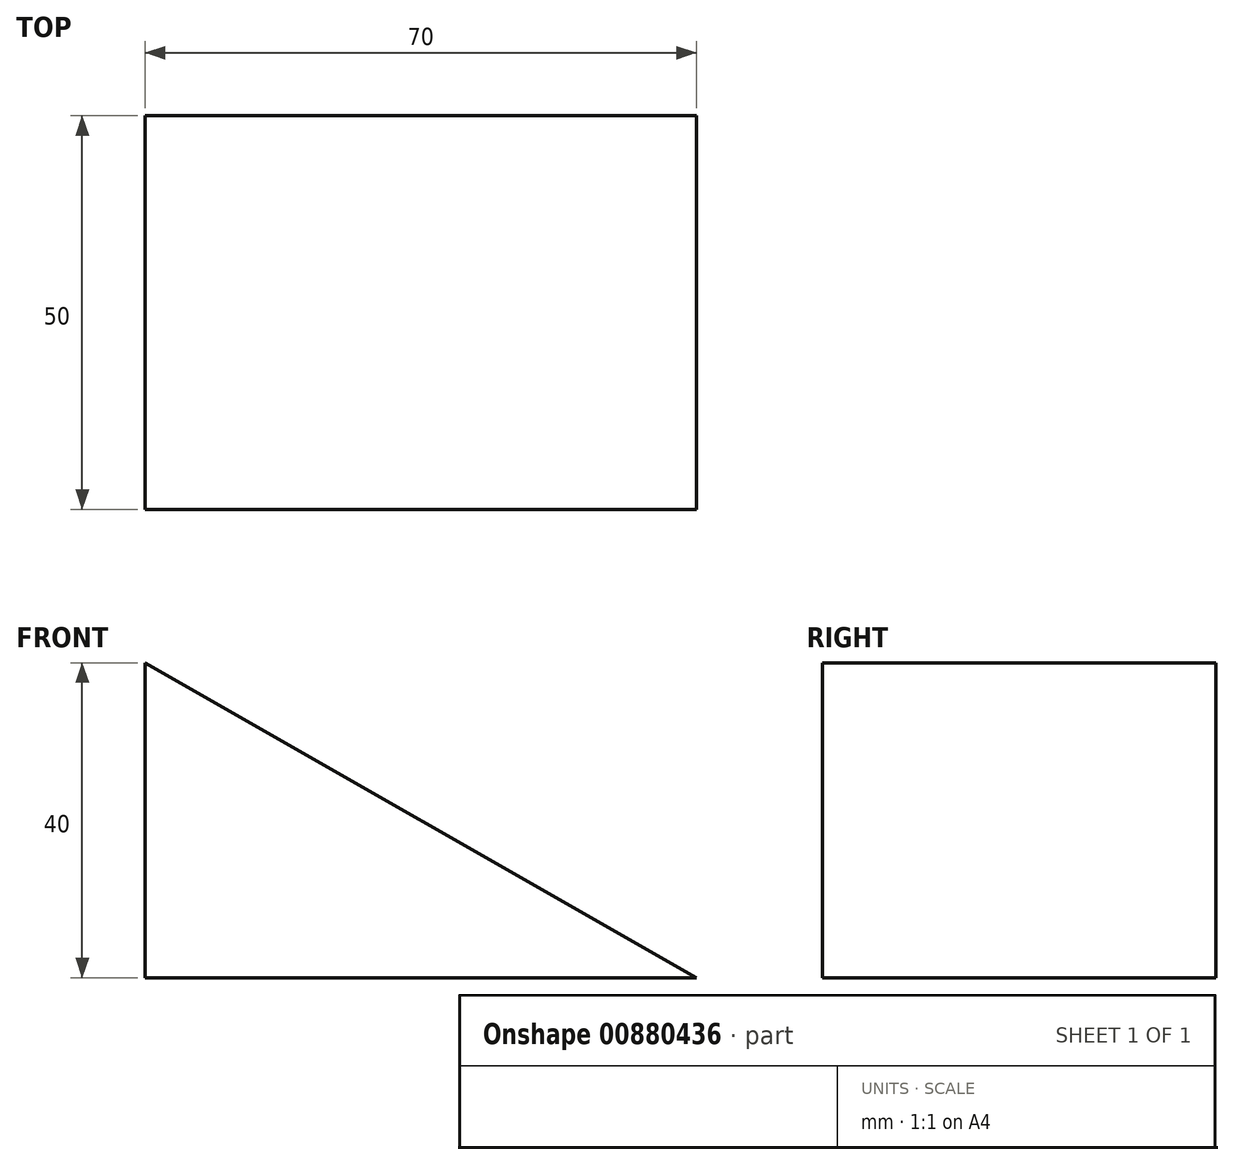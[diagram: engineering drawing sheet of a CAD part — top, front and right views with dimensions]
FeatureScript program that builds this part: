
annotation { "Feature Type Name" : "Feature", "Feature Type Description" : "" }
export const myFeature = defineFeature(function(context is Context, id is Id, definition is map)
    precondition{}
    {
        {
            var Q0;
            Q0=qCreatedBy(makeId("Front.planeOp"),FACE);
            var sketch = newSketch(context, id + "F0", { "sketchPlane" : qUnion([Q0])});
            skLineSegment(sketch, "E0", {"start": v(0, 0) * mm, "end": v(0, 40) * mm});
            skLineSegment(sketch, "E1", {"start": v(0, 40) * mm, "end": v(70, 0) * mm});
            skLineSegment(sketch, "E2", {"start": v(70, 0) * mm, "end": v(0, 0) * mm});
            skSolve(sketch);
        }
        {
            var Q0;
            Q0=makeQuery(id+"F0.imprint","IMPRINT",FACE,{"disambiguationData":[TD([[makeQuery(id+"F0.imprint","IMPRINT",EDGE,{"derivedFrom":sQuery(id+"F0.wireOp",EDGE,"E0")}),-1.0]])]});
            extrude(context, id + "F1", {"entities" : qUnion([Q0]), "depth" : 50 * mm, "offsetDistance" : 25 * mm});
        }
    });
